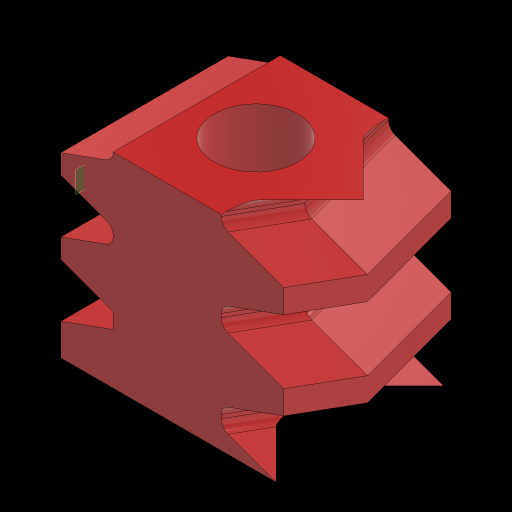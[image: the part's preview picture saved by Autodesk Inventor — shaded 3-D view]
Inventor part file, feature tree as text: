
AUTODESK INVENTOR PART (.ipt)
format: ipt  version: 2023.2 (Build 272271030, 271C)  size: 502,784 bytes
history: native  units: mm
features: sketch x5, extrude x3, projected_geometry x3, plane x2, sweep x1, pattern_linear x1, mirror x1
ambient origin geometry x8: Origin, YZ Plane, XZ Plane, XY Plane, X Axis, Y Axis, Z Axis, Center Point
bodies: Solid1 (feature_tree)
feature tree (16):
  extrude  "Extrusion1"  Depth=11.0mm
  sweep  "Sweep1"
  pattern_linear  "Rectangular Pattern2"  Spacing1=1.5mm  [1 undecoded]
  mirror  "Mirror2"
  plane  "Work Plane3"
  extrude  "Extrusion4"  Depth=4.5mm
  plane  "Work Plane4"
  extrude  "Extrusion5"  TaperAngle=0.0deg  [1 undecoded]
  sketch  "Sketch1"  dims[d0=12.0mm d1=11.0mm]
  sketch  "Sketch2"  dims[d2=4.5mm d3=0.0mm d14=12.217305mm]
  projected_geometry  "Projected Loop1"
  sketch  "Sketch3"  dims[d15=4.712389mm]
  projected_geometry  "Projected Loop2"
  sketch  "Sketch6"  dims[d16=0.57mm]
  projected_geometry  "Projected Loop5"
  sketch  "Sketch7"  dims[d17=3.375mm d18=1.5mm d19=2.356194mm d22=0.0mm d23=0.0mm d27=80.0mm d29=4.7124mm d31=3.490659mm d32=3.577925mm d48=2.356194mm d49=-1.5mm d50=12.217305mm d51=1.25mm d52=1.5625mm d53=1.963495mm d54=0.475mm d55=40.0mm d57=22.5deg d58=10.0mm d60=10.0mm d62=10.0mm d63=0.0mm d64=-1.25mm d65=4.5mm d66=0.0mm d67=0.0mm]
note: 2 required parameter values undecoded (feature->parameter linkage not recoverable at this tier; creation-order binding heuristic only, values carry confidence <= 0.55)
